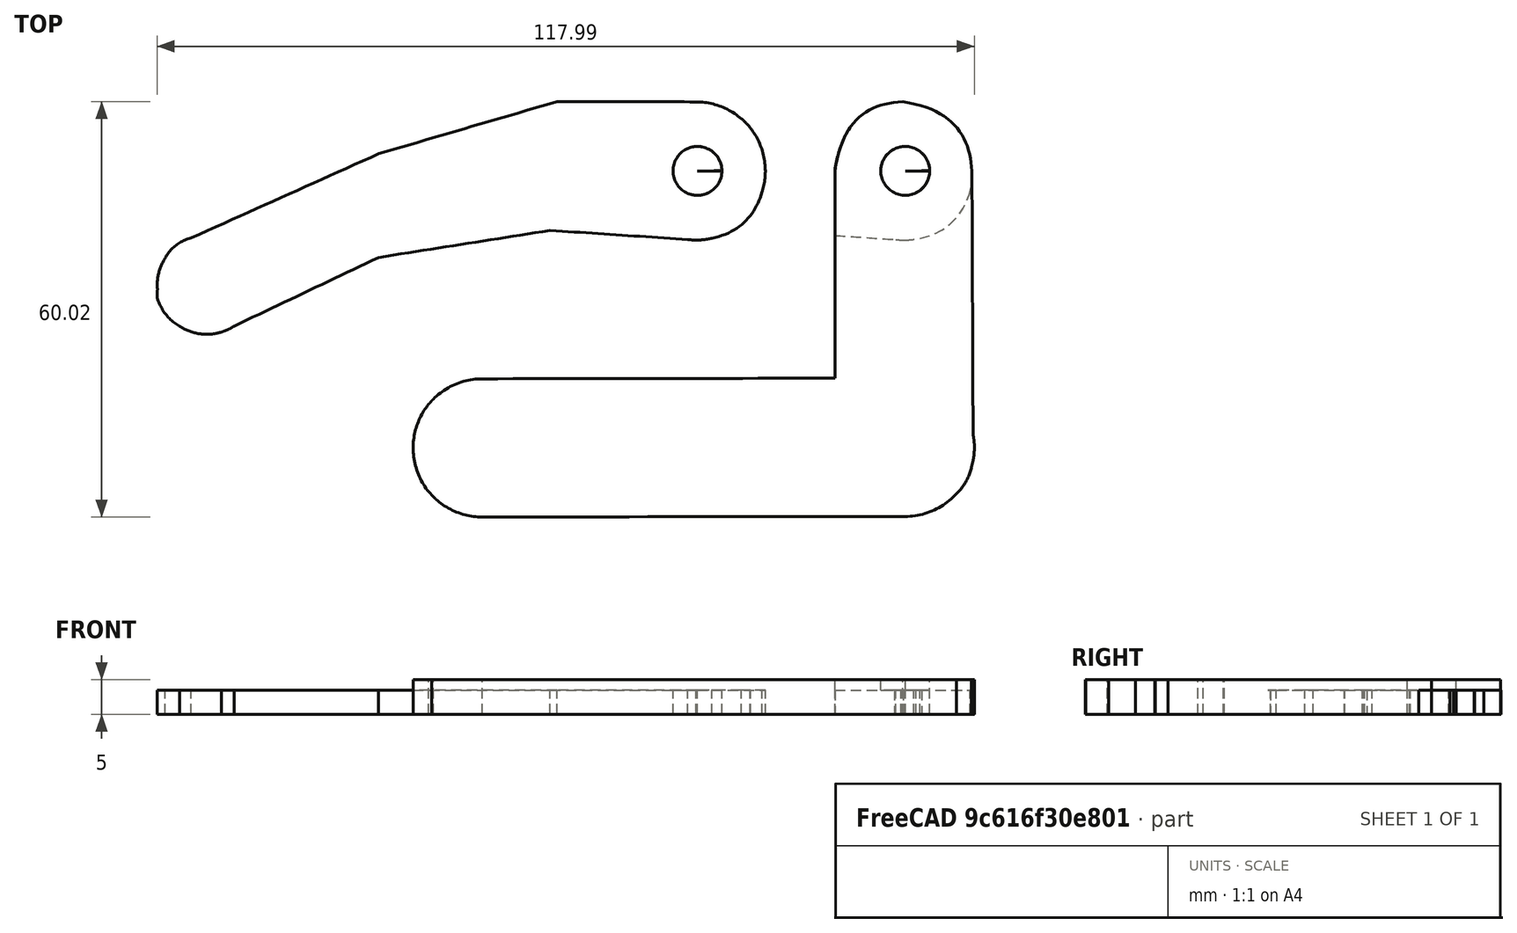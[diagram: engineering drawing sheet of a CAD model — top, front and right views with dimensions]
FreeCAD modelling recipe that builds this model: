
FCSTD DOCUMENT  (FreeCAD 0.20R29410 (Git))
Label: pinza_buena
License: Creative Commons Attribution
LicenseURL: http://creativecommons.org/licenses/by/4.0/
objects: Part::Feature×6, Part::Extrusion×6, Part::Cut×4
note: 16 computed .brp shape members not serialized (recipe doc carries the construction recipe); baked Part::Feature solids carry a one-line shape summary decoded from their .brp

FEATURE [Part::Feature] path2258_5
  shape: bbox 87.81 x 33.62 x 2e-07 mm, 1 faces, 0 solids (baked)
FEATURE [Part::Feature] path2258_5001
  shape: bbox 7.059 x 7.06 x 2e-07 mm, 1 faces, 0 solids (baked)
FEATURE [Part::Feature] path2258
  shape: bbox 81.02 x 59.99 x 2e-07 mm, 1 faces, 0 solids (baked)
FEATURE [Part::Feature] path2258001
  shape: bbox 7.059 x 7.06 x 2e-07 mm, 1 faces, 0 solids (baked)
FEATURE [Part::Extrusion] Extrude
  Base = -> path2258001
  Dir = (0,0,1)
  DirMode = 0
  FaceMakerClass = Part::FaceMakerBullseye
  LengthFwd = 5
  LengthRev = 0
  Solid = false
  Symmetric = false
FEATURE [Part::Extrusion] Extrude001
  Base = -> path2258
  Dir = (0,0,1)
  DirMode = 0
  FaceMakerClass = Part::FaceMakerBullseye
  LengthFwd = 5
  LengthRev = 0
  Solid = false
  Symmetric = false
FEATURE [Part::Extrusion] Extrude002
  Base = -> path2258_5001
  Dir = (0,0,1)
  DirMode = 0
  FaceMakerClass = Part::FaceMakerBullseye
  LengthFwd = 5
  LengthRev = 0
  Solid = false
  Symmetric = false
FEATURE [Part::Extrusion] Extrude003
  Base = -> path2258_5
  Dir = (0,0,1)
  DirMode = 0
  FaceMakerClass = Part::FaceMakerBullseye
  LengthFwd = 3.5
  LengthRev = 0
  Solid = false
  Symmetric = false
FEATURE [Part::Cut] Cut
  Base = -> Extrude001
  Refine = true
  Tool = -> Extrude
FEATURE [Part::Cut] Cut001
  Base = -> Extrude003
  Refine = true
  Tool = -> Extrude002
FEATURE [Part::Feature] path2258_5002
  shape: bbox 87.81 x 33.62 x 2e-07 mm, 1 faces, 0 solids (baked)
FEATURE [Part::Extrusion] Extrude005
  Base = -> path2258_5002
  Dir = (0,0,1)
  DirMode = 0
  FaceMakerClass = Part::FaceMakerBullseye
  LengthFwd = 3.5
  LengthRev = 0
  Solid = false
  Symmetric = false
FEATURE [Part::Feature] path2258_5003
  shape: bbox 7.059 x 7.06 x 2e-07 mm, 1 faces, 0 solids (baked)
FEATURE [Part::Extrusion] Extrude004
  Base = -> path2258_5003
  Dir = (0,0,1)
  DirMode = 0
  FaceMakerClass = Part::FaceMakerBullseye
  LengthFwd = 5
  LengthRev = 0
  Solid = false
  Symmetric = false
FEATURE [Part::Cut] Cut002
  Base = -> Extrude005
  Placement = pos=(-30,0,0) rot=(0,0,1;0rad)
  Refine = true
  Tool = -> Extrude004
FEATURE [Part::Cut] Cut003
  Base = -> Cut
  Refine = true
  Tool = -> Cut001
